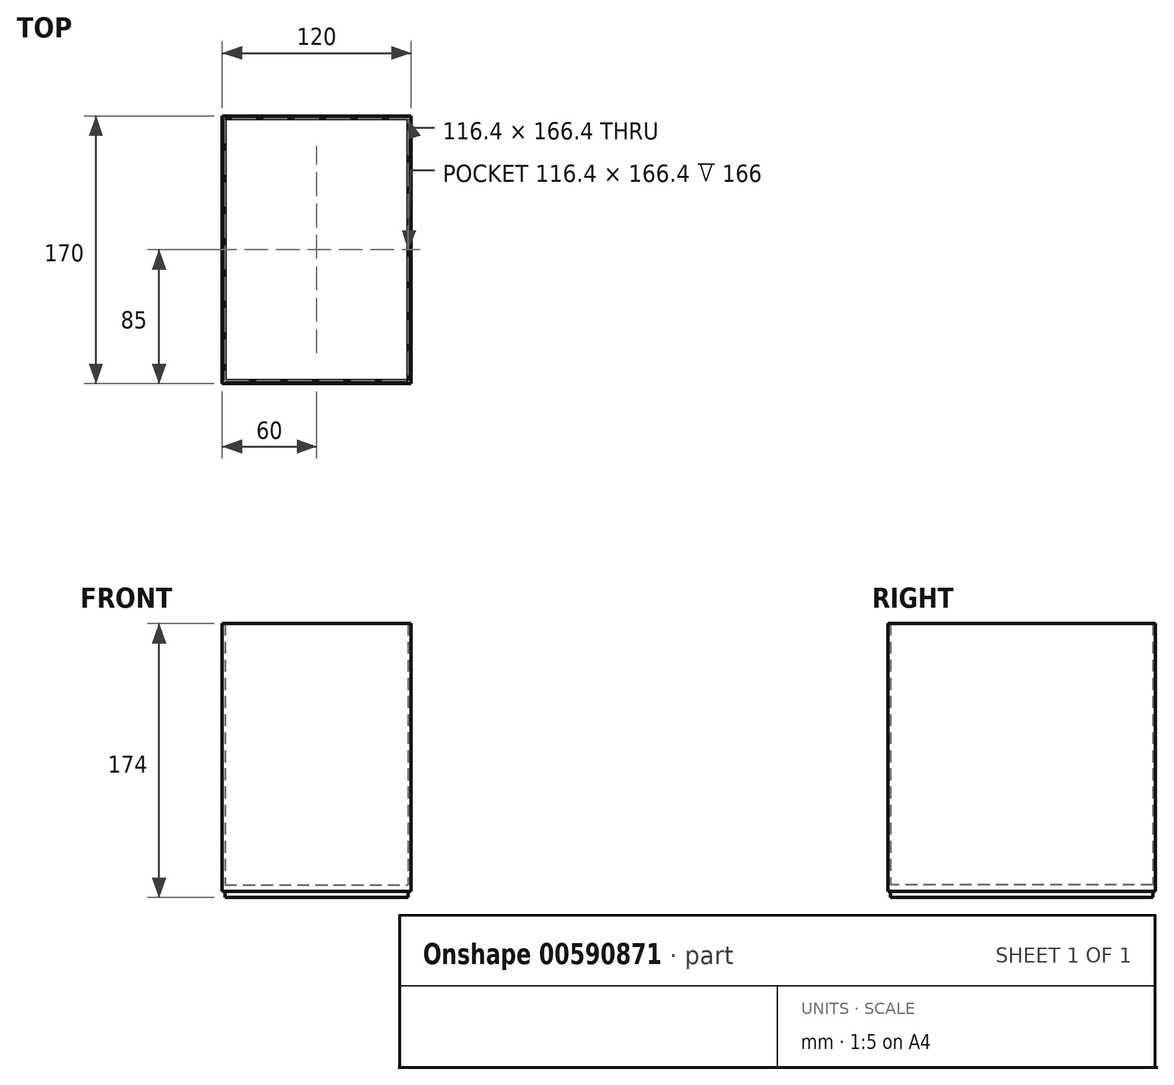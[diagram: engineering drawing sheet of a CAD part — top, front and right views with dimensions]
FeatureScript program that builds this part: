
annotation { "Feature Type Name" : "Feature", "Feature Type Description" : "" }
export const myFeature = defineFeature(function(context is Context, id is Id, definition is map)
    precondition{}
    {
        {
            var Q0;
            Q0=qCreatedBy(makeId("Top.planeOp"),FACE);
            var sketch = newSketch(context, id + "F0", { "sketchPlane" : qUnion([Q0])});
            skLineSegment(sketch, "E0.bottom", {"start": v(-60, 85) * mm, "end": v(60, 85) * mm});
            skLineSegment(sketch, "E0.top", {"start": v(-60, -85) * mm, "end": v(60, -85) * mm});
            skLineSegment(sketch, "E0.left", {"start": v(-60, 85) * mm, "end": v(-60, -85) * mm});
            skLineSegment(sketch, "E0.right", {"start": v(60, 85) * mm, "end": v(60, -85) * mm});
            skPoint(sketch, "E0.middle", {"position": v(0, 0) * mm});
            skLineSegment(sketch, "E1.0", {"start": v(-58.2, 83.2) * mm, "end": v(-58.2, -83.2) * mm});
            skLineSegment(sketch, "E1.1", {"start": v(-58.2, 83.2) * mm, "end": v(58.2, 83.2) * mm});
            skLineSegment(sketch, "E1.2", {"start": v(58.2, 83.2) * mm, "end": v(58.2, -83.2) * mm});
            skLineSegment(sketch, "E1.3", {"start": v(-58.2, -83.2) * mm, "end": v(58.2, -83.2) * mm});
            skSolve(sketch);
        }
        {
            var Q0;
            Q0=makeQuery(id+"F0.imprint","IMPRINT",FACE,{"disambiguationData":[TD([[makeQuery(id+"F0.imprint","IMPRINT",EDGE,{"derivedFrom":sQuery(id+"F0.wireOp",EDGE,"E0.bottom")}),-1.0]])]});
            extrude(context, id + "F1", {"entities" : qUnion([Q0]), "depth" : 170 * mm, "offsetDistance" : 25 * mm});
        }
        {
            var Q0;
            Q0=makeQuery(id+"F0.imprint","IMPRINT",FACE,{"disambiguationData":[TD([[makeQuery(id+"F0.imprint","IMPRINT",EDGE,{"derivedFrom":sQuery(id+"F0.wireOp",EDGE,"E1.0")}),1.0]])]});
            extrude(context, id + "F2", {"entities" : qUnion([Q0]), "operationType" : NewBodyOperationType.ADD, "endBound" : BoundingType.SYMMETRIC, "depth" : 8 * mm, "offsetDistance" : 25 * mm});
        }
    });
